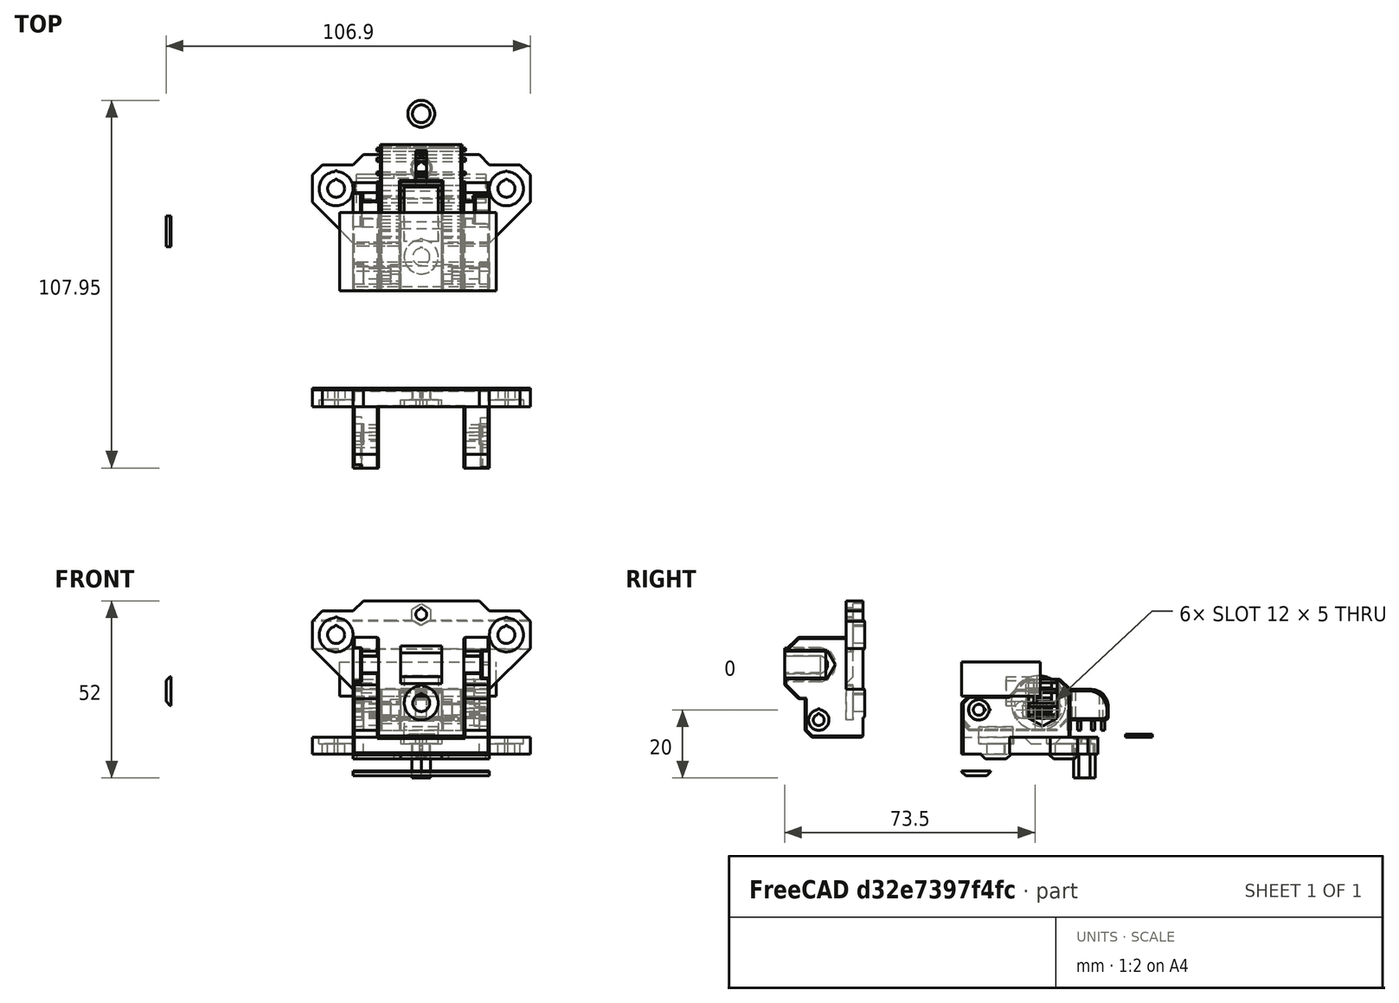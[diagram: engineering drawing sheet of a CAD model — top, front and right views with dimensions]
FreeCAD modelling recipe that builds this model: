
FCSTD DOCUMENT  (FreeCAD 0.18R14555 (Git shallow))
Label: y-idler-10mm-lower
License: All rights reserved
LicenseURL: http://en.wikipedia.org/wiki/All_rights_reserved
objects: Part::Box×62, Part::Cylinder×39, Part::Cut×31, Part::MultiFuse×30, Part::Chamfer×24, Part::Feature×21, Part::MultiCommon×1, Part::Fillet×1
note: 209 computed .brp shape members not serialized (recipe doc carries the construction recipe); baked Part::Feature solids carry a one-line shape summary decoded from their .brp

FEATURE [Part::Box] Box  label="Cube"
  AttacherType = Attacher::AttachEngine3D
  Height = 10
  Length = 40
  Placement = pos=(-20,-20,-10) rot=(0,0,1;0rad)
  Width = 40
FEATURE [Part::Box] Box001  label="Cube001"
  AttacherType = Attacher::AttachEngine3D
  Height = 12
  Length = 6
  Placement = pos=(6,-20,4) rot=(0,0,1;0rad)
  Width = 43
FEATURE [Part::Box] Box002  label="Cube002"
  AttacherType = Attacher::AttachEngine3D
  Height = 12
  Length = 6
  Placement = pos=(-12,-20,4) rot=(0,0,1;0rad)
  Width = 43
FEATURE [Part::Box] Box003  label="Cube003"
  AttacherType = Attacher::AttachEngine3D
  Height = 12
  Length = 12
  Placement = pos=(-6,12,2) rot=(0,0,1;0rad)
  Width = 11
FEATURE [Part::Cylinder] Cylinder  label="idler"
  Angle = 360
  AttacherType = Attacher::AttachEngine3D
  Height = 10
  Placement = pos=(5,2.54,10) rot=(0,-1,0;1.5708rad)
  Radius = 8
FEATURE [Part::Cylinder] Cylinder001
  Angle = 360
  AttacherType = Attacher::AttachEngine3D
  Height = 6
  Placement = pos=(6,-2,15) rot=(0,1,0;1.5708rad)
  Radius = 2.5
FEATURE [Part::Cylinder] Cylinder002
  Angle = 360
  AttacherType = Attacher::AttachEngine3D
  Height = 6
  Placement = pos=(-12,5,15) rot=(0,1,0;1.5708rad)
  Radius = 2.5
FEATURE [Part::Cylinder] Cylinder003
  Angle = 360
  AttacherType = Attacher::AttachEngine3D
  Height = 6
  Placement = pos=(-12,-2,15) rot=(0,1,0;1.5708rad)
  Radius = 2.5
FEATURE [Part::Cylinder] Cylinder004
  Angle = 360
  AttacherType = Attacher::AttachEngine3D
  Height = 6
  Placement = pos=(6,5,15) rot=(0,1,0;1.5708rad)
  Radius = 2.5
FEATURE [Part::Box] Box005  label="Cube005"
  AttacherType = Attacher::AttachEngine3D
  Height = 5
  Length = 6
  Placement = pos=(6,-2,12.5) rot=(0,0,1;0rad)
  Width = 7
FEATURE [Part::Box] Box006  label="Cube006"
  AttacherType = Attacher::AttachEngine3D
  Height = 5
  Length = 6
  Placement = pos=(-12,-2,12.5) rot=(0,0,1;0rad)
  Width = 7
FEATURE [Part::MultiFuse] Fusion
  Placement = pos=(0,2,-5) rot=(0,0,1;0rad)
  Shapes = -> [Box005,Cylinder001,Cylinder004]
FEATURE [Part::MultiFuse] Fusion001
  Placement = pos=(0,2,-5) rot=(0,0,1;0rad)
  Shapes = -> [Box006,Cylinder003,Cylinder002]
FEATURE [Part::Box] Box007  label="Cube007"
  AttacherType = Attacher::AttachEngine3D
  Height = 12
  Length = 7.5
  Placement = pos=(-20,-20,0) rot=(0,0,1;0rad)
  Width = 14
FEATURE [Part::Box] Box008  label="Cube008"
  AttacherType = Attacher::AttachEngine3D
  Height = 12
  Length = 7.5
  Placement = pos=(12.5,-20,0) rot=(0,0,1;0rad)
  Width = 14
FEATURE [Part::Box] Box009  label="Cube009"
  AttacherType = Attacher::AttachEngine3D
  Height = 20
  Length = 7.5
  Placement = pos=(-20,-10,0) rot=(0,0,1;0rad)
  Width = 18
FEATURE [Part::Box] Box010  label="Cube010"
  AttacherType = Attacher::AttachEngine3D
  Height = 20
  Length = 7.5
  Placement = pos=(12.5,-10,0) rot=(0,0,1;0rad)
  Width = 18
FEATURE [Part::Chamfer] Chamfer
  Base = -> Box009
  Edges = 2 edges r=4: [Edge10,Edge12]
FEATURE [Part::Chamfer] Chamfer001
  Base = -> Box010
  Edges = 2 edges r=4: [Edge10,Edge12]
FEATURE [Part::Cylinder] Cylinder005  label="Cylinder"
  Angle = 360
  AttacherType = Attacher::AttachEngine3D
  Height = 8
  Placement = pos=(-12,0,10) rot=(0,-1,0;1.5708rad)
  Radius = 2.6
FEATURE [Part::Cylinder] Cylinder006  label="Cylinder005"
  Angle = 360
  AttacherType = Attacher::AttachEngine3D
  Height = 8
  Placement = pos=(20,0,10) rot=(0,-1,0;1.5708rad)
  Radius = 2.6
FEATURE [Part::Box] Box011  label="Cube011"
  AttacherType = Attacher::AttachEngine3D
  Height = 10
  Length = 8
  Placement = pos=(12,-2.6,10) rot=(0,0,1;0rad)
  Width = 5.2
FEATURE [Part::Box] Box012  label="Cube012"
  AttacherType = Attacher::AttachEngine3D
  Height = 10
  Length = 8
  Placement = pos=(-20,-2.6,10) rot=(0,0,1;0rad)
  Width = 5.2
FEATURE [Part::Cylinder] Cylinder007  label="Cylinder006"
  Angle = 360
  AttacherType = Attacher::AttachEngine3D
  Height = 31
  Placement = pos=(0,16,-10) rot=(0,0,1;0rad)
  Radius = 1.6
FEATURE [Part::Box] Box013  label="Cube013"
  AttacherType = Attacher::AttachEngine3D
  Height = 30
  Length = 3.2
  Placement = pos=(-1.6,13.5,0) rot=(0,0,1;0rad)
  Width = 8
FEATURE [Part::Cylinder] Cylinder008  label="Cylinder007"
  Angle = 360
  AttacherType = Attacher::AttachEngine3D
  Height = 3
  Placement = pos=(25,10,-3) rot=(0,0,1;0rad)
  Radius = 5
FEATURE [Part::Cylinder] Cylinder009  label="Cylinder008"
  Angle = 360
  AttacherType = Attacher::AttachEngine3D
  Height = 8
  Placement = pos=(-12,-15,10) rot=(0,-1,0;1.5708rad)
  Radius = 1.6
FEATURE [Part::Cylinder] Cylinder010  label="Cylinder009"
  Angle = 360
  AttacherType = Attacher::AttachEngine3D
  Height = 8
  Placement = pos=(20,-15,10) rot=(0,-1,0;1.5708rad)
  Radius = 1.6
FEATURE [Part::Cylinder] Cylinder011  label="Cylinder010"
  Angle = 360
  AttacherType = Attacher::AttachEngine3D
  Height = 24
  Placement = pos=(12,-15,10) rot=(0,-1,0;1.5708rad)
  Radius = 1.6
FEATURE [Part::Cylinder] Cylinder012  label="Cylinder011"
  Angle = 360
  AttacherType = Attacher::AttachEngine3D
  Height = 3
  Placement = pos=(-25,10,-3) rot=(0,0,1;0rad)
  Radius = 5
FEATURE [Part::Box] Box014  label="Cube014"
  AttacherType = Attacher::AttachEngine3D
  Height = 10
  Length = 64
  Placement = pos=(-32,-6,-10) rot=(0,0,1;0rad)
  Width = 23
FEATURE [Part::Chamfer] Chamfer004
  Base = -> Box014
  Edges = 2 edges r=12: [Edge1,Edge5]
FEATURE [Part::Chamfer] Chamfer005
  Base = -> Box
  Edges = 2 edges r=3: [Edge3,Edge7]
FEATURE [Part::Chamfer] Chamfer006
  Base = -> Chamfer004
  Edges = 2 edges r=3: [Edge3,Edge13]
FEATURE [Part::Cylinder] Cylinder013  label="Cylinder012"
  Angle = 360
  AttacherType = Attacher::AttachEngine3D
  Height = 24
  Placement = pos=(12,-15,11.4) rot=(0,-1,0;1.5708rad)
  Radius = 0.5
FEATURE [Part::Cylinder] Cylinder014  label="Cylinder013"
  Angle = 360
  AttacherType = Attacher::AttachEngine3D
  Height = 8
  Placement = pos=(20,-13.6,10) rot=(0,-1,0;1.5708rad)
  Radius = 0.5
FEATURE [Part::Cylinder] Cylinder015  label="Cylinder014"
  Angle = 360
  AttacherType = Attacher::AttachEngine3D
  Height = 8
  Placement = pos=(-12,-13.6,10) rot=(0,-1,0;1.5708rad)
  Radius = 0.5
FEATURE [Part::Cylinder] Cylinder016  label="Cylinder015"
  Angle = 360
  AttacherType = Attacher::AttachEngine3D
  Height = 15
  Placement = pos=(-25,10,-10) rot=(0,0,1;0rad)
  Radius = 2.5
FEATURE [Part::Cylinder] Cylinder017  label="Cylinder016"
  Angle = 360
  AttacherType = Attacher::AttachEngine3D
  Height = 15
  Placement = pos=(25,10,-10) rot=(0,0,1;0rad)
  Radius = 2.5
FEATURE [Part::Cylinder] Cylinder018  label="Cylinder019"
  Angle = 360
  AttacherType = Attacher::AttachEngine3D
  Height = 15
  Placement = pos=(25,12.3,-10) rot=(0,0,1;0rad)
  Radius = 0.5
FEATURE [Part::Cylinder] Cylinder019  label="Cylinder020"
  Angle = 360
  AttacherType = Attacher::AttachEngine3D
  Height = 15
  Placement = pos=(-25,12.3,-10) rot=(0,0,1;0rad)
  Radius = 0.5
FEATURE [Part::Cylinder] Cylinder020  label="Cylinder021"
  Angle = 360
  AttacherType = Attacher::AttachEngine3D
  Height = 31
  Placement = pos=(0,17.4,-10) rot=(0,0,1;0rad)
  Radius = 0.5
FEATURE [Part::Cylinder] Cylinder021  label="Cylinder022"
  Angle = 360
  AttacherType = Attacher::AttachEngine3D
  Height = 15
  Placement = pos=(0,-10,-10) rot=(0,0,1;0rad)
  Radius = 2.5
FEATURE [Part::Cylinder] Cylinder022  label="Cylinder023"
  Angle = 360
  AttacherType = Attacher::AttachEngine3D
  Height = 3
  Placement = pos=(0,-10,0) rot=(0,0,1;0rad)
  Radius = 5
FEATURE [Part::Cylinder] Cylinder023  label="Cylinder024"
  Angle = 360
  AttacherType = Attacher::AttachEngine3D
  Height = 15
  Placement = pos=(0,-7.7,-10) rot=(0,0,1;0rad)
  Radius = 0.5
FEATURE [Part::MultiFuse] Fusion006
  Placement = pos=(0,0,-5) rot=(0,0,1;0rad)
  Shapes = -> [Cylinder023,Cylinder017,Cylinder021,Cylinder018,Cylinder020,Cylinder007,Cylinder016,Cylinder019]
FEATURE [Part::Cylinder] Cylinder024  label="Cylinder025"
  Angle = 360
  AttacherType = Attacher::AttachEngine3D
  Height = 2.5
  Placement = pos=(-17.5,0,10) rot=(0,-1,0;1.5708rad)
  Radius = 5
FEATURE [Part::Box] Box015  label="Cube015"
  AttacherType = Attacher::AttachEngine3D
  Height = 10
  Length = 2.5
  Placement = pos=(-20,-5,10) rot=(0,0,1;0rad)
  Width = 10
FEATURE [Part::Feature] Part__Feature  label="y_motor_mount v18"
  Placement = pos=(-68,0,0) rot=(0,0,1;0rad)
  shape: bbox 62 x 21 x 44 mm, 162 faces (baked)
FEATURE [Part::Box] Box016  label="Cube016"
  AttacherType = Attacher::AttachEngine3D
  Height = 10
  Length = 10
  Placement = pos=(-83.5,-7,9) rot=(0,0,1;0rad)
  Width = 9
FEATURE [Part::MultiCommon] Common
  Shapes = -> [Part__Feature,Box016]
FEATURE [Part::Feature] Common001
  Placement = pos=(13,-2.27,63.5) rot=(0.57735,-0.57735,0.57735;2.0944rad)
  shape: bbox 9 x 8.45 x 1.4 mm, 8 faces (baked)
FEATURE [Part::Feature] Common002
  Placement = pos=(4,-2.27,63.5) rot=(0.57735,-0.57735,0.57735;2.0944rad)
  shape: bbox 9 x 8.45 x 1.4 mm, 8 faces (baked)
FEATURE [Part::Feature] Common003
  Placement = pos=(-5,-2.27,63.5) rot=(0.57735,-0.57735,0.57735;2.0944rad)
  shape: bbox 9 x 8.45 x 1.4 mm, 8 faces (baked)
FEATURE [Part::Feature] Common004
  Placement = pos=(-14,-2.27,63.5) rot=(0.57735,-0.57735,0.57735;2.0944rad)
  shape: bbox 9 x 8.45 x 1.4 mm, 8 faces (baked)
FEATURE [Part::Feature] Common005
  Placement = pos=(-18,-2.27,63.5) rot=(0.57735,-0.57735,0.57735;2.0944rad)
  shape: bbox 9 x 8.45 x 1.4 mm, 8 faces (baked)
FEATURE [Part::MultiFuse] Fusion010
  Shapes = -> [Common001,Common002,Common003,Common005,Common004]
FEATURE [Part::Feature] Fusion010001  label="Fusion011"
  Placement = pos=(0,5.775,5) rot=(0,0,1;0rad)
  shape: bbox 40 x 8.45 x 1.4 mm, 38 faces (baked)
FEATURE [Part::Feature] Fusion010002  label="Fusion012"
  Placement = pos=(12,25.77,5) rot=(0,0,1;0rad)
  shape: bbox 40 x 8.45 x 1.4 mm, 38 faces (baked)
FEATURE [Part::Feature] Fusion010003  label="Fusion013"
  Placement = pos=(-12,25.765,5) rot=(0,0,1;0rad)
  shape: bbox 40 x 8.45 x 1.4 mm, 38 faces (baked)
FEATURE [Part::Cylinder] Cylinder025  label="Cylinder026"
  Angle = 360
  AttacherType = Attacher::AttachEngine3D
  Height = 3
  Placement = pos=(0,-10,-3) rot=(0,0,1;0rad)
  Radius = 5
FEATURE [Part::Cylinder] Cylinder026  label="Cylinder027"
  Angle = 360
  AttacherType = Attacher::AttachEngine3D
  Height = 3
  Placement = pos=(0,-5.2,-3) rot=(0,0,1;0rad)
  Radius = 0.5
FEATURE [Part::Cylinder] Cylinder027  label="Cylinder028"
  Angle = 360
  AttacherType = Attacher::AttachEngine3D
  Height = 3
  Placement = pos=(-25,14.8,-3) rot=(0,0,1;0rad)
  Radius = 0.5
FEATURE [Part::Cylinder] Cylinder028  label="Cylinder029"
  Angle = 360
  AttacherType = Attacher::AttachEngine3D
  Height = 3
  Placement = pos=(25,14.7,-3) rot=(0,0,1;0rad)
  Radius = 0.5
FEATURE [Part::MultiFuse] Fusion010005
  Shapes = -> [Cylinder025,Cylinder012,Cylinder008]
FEATURE [Part::Box] Box017  label="Cube017"
  AttacherType = Attacher::AttachEngine3D
  Height = 10
  Length = 10
  Placement = pos=(-60,0,-20) rot=(0,0,1;0rad)
  Width = 10
FEATURE [Part::Box] Box018  label="Cube018"
  AttacherType = Attacher::AttachEngine3D
  Height = 10
  Length = 10
  Placement = pos=(-40,0,-20) rot=(0,0,1;0rad)
  Width = 10
FEATURE [Part::Box] Box019  label="Cube019"
  AttacherType = Attacher::AttachEngine3D
  Height = 10
  Length = 10
  Placement = pos=(40,0,-20) rot=(0,0,1;0rad)
  Width = 10
FEATURE [Part::Box] Box020  label="Cube020"
  AttacherType = Attacher::AttachEngine3D
  Height = 10
  Length = 10
  Placement = pos=(40,0,-20) rot=(0,0,1;0rad)
  Width = 10
FEATURE [Part::Chamfer] Chamfer016
  Base = -> Box018
  Edges = 1 edges r=4: [Edge5]
  Placement = pos=(0,12,5) rot=(0,0,1;0rad)
FEATURE [Part::Chamfer] Chamfer017
  Base = -> Box017
  Edges = 1 edges r=4: [Edge7]
  Placement = pos=(20,-2,5) rot=(0,0,1;0rad)
FEATURE [Part::Chamfer] Chamfer018
  Base = -> Box019
  Edges = 1 edges r=4: [Edge3]
  Placement = pos=(-11,-3,5) rot=(0,0,1;0rad)
FEATURE [Part::Chamfer] Chamfer019
  Base = -> Box020
  Edges = 1 edges r=4: [Edge1]
  Placement = pos=(-9,11,5) rot=(0,0,1;0rad)
FEATURE [Part::Cylinder] Cylinder030  label="Cylinder031"
  Angle = 360
  AttacherType = Attacher::AttachEngine3D
  Height = 3
  Placement = pos=(-20,-12.2,10) rot=(0,1,0;1.5708rad)
  Radius = 0.5
FEATURE [Part::Cylinder] Cylinder031  label="Cylinder032"
  Angle = 360
  AttacherType = Attacher::AttachEngine3D
  Height = 3
  Placement = pos=(-20,-15,10) rot=(0,1,0;1.5708rad)
  Radius = 3
FEATURE [Part::Feature] Body005001  label="Body006"
  Placement = pos=(-9,-15,10) rot=(1,0,0;1.5708rad)
  shape: bbox 3 x 5.543 x 6.4 mm, 8 faces (baked)
FEATURE [Part::Cylinder] Cylinder032  label="Cylinder033"
  Angle = 360
  AttacherType = Attacher::AttachEngine3D
  Height = 3
  Placement = pos=(17,-15,10) rot=(0,1,0;1.5708rad)
  Radius = 3
FEATURE [Part::Cylinder] Cylinder033  label="Cylinder034"
  Angle = 360
  AttacherType = Attacher::AttachEngine3D
  Height = 3
  Placement = pos=(17,-12.2,10) rot=(0,1,0;1.5708rad)
  Radius = 0.5
FEATURE [Part::MultiFuse] Fusion010006003
  Shapes = -> [Cylinder031,Cylinder030]
FEATURE [Part::MultiFuse] Fusion010006004
  Shapes = -> [Cylinder033,Cylinder032]
FEATURE [Part::Feature] Body005002  label="Body007"
  Placement = pos=(6,-15,10) rot=(1,0,0;1.5708rad)
  shape: bbox 3 x 5.543 x 6.4 mm, 8 faces (baked)
FEATURE [Part::Feature] Body005003001  label="Body005004"
  Placement = pos=(0,16,-12) rot=(0,0,1;0rad)
  shape: bbox 5.543 x 6.4 x 10 mm, 8 faces (baked)
FEATURE [Part::Cylinder] Cylinder034  label="Cylinder035"
  Angle = 360
  AttacherType = Attacher::AttachEngine3D
  Height = 0.5
  Placement = pos=(0,16,-0.5) rot=(0,0,1;0rad)
  Radius = 3.2
FEATURE [Part::Cylinder] Cylinder035  label="Cylinder036"
  Angle = 360
  AttacherType = Attacher::AttachEngine3D
  Height = 0.5
  Placement = pos=(0,19,-0.5) rot=(0,0,1;0rad)
  Radius = 0.5
FEATURE [Part::MultiFuse] Fusion010006005
  Shapes = -> [Cylinder035,Cylinder034]
FEATURE [Part::Box] Box029  label="Cube029"
  AttacherType = Attacher::AttachEngine3D
  Height = 1
  Length = 2.1
  Placement = pos=(-20,-3.53,7.5) rot=(0,0,1;0rad)
  Width = 9.6
FEATURE [Part::Box] Box030  label="Cube030"
  AttacherType = Attacher::AttachEngine3D
  Height = 1
  Length = 4.1
  Placement = pos=(15.9,-2.68,5.6) rot=(0,0,1;0rad)
  Width = 7.91
FEATURE [Part::Box] Box032  label="Cube032"
  AttacherType = Attacher::AttachEngine3D
  Height = 1
  Length = 5
  Placement = pos=(-17.5,-1.13,7.5) rot=(0,0,1;0rad)
  Width = 4.8
FEATURE [Part::MultiFuse] Fusion010006008
  Shapes = -> [Box012,Cylinder005]
FEATURE [Part::MultiFuse] Fusion010006009
  Shapes = -> [Cylinder006,Box011]
FEATURE [Part::Cut] Cut022015
  Base = -> Chamfer
  Tool = -> Fusion010006008
FEATURE [Part::Cut] Cut022016
  Base = -> Chamfer001
  Tool = -> Fusion010006009
FEATURE [Part::Feature] Pad002001  label="Pad003"
  Placement = pos=(17.5,0,10) rot=(0.57735,0.57735,0.57735;2.0944rad)
  shape: bbox 10 x 8.314 x 9.6 mm, 8 faces (baked)
FEATURE [Part::Feature] Pad002002  label="Pad004"
  Placement = pos=(17.5,0,14) rot=(0.57735,0.57735,0.57735;2.0944rad)
  shape: bbox 10 x 8.314 x 9.6 mm, 8 faces (baked)
FEATURE [Part::Feature] Pad002003  label="Pad005"
  Placement = pos=(17.5,0,18) rot=(0.57735,0.57735,0.57735;2.0944rad)
  shape: bbox 10 x 8.314 x 9.6 mm, 8 faces (baked)
FEATURE [Part::MultiFuse] Fusion010006010
  Shapes = -> [Pad002003,Pad002001,Pad002002]
FEATURE [Part::Cut] Cut022017  label="base-right-arm-top"
  Base = -> Cut022016
  Placement = pos=(0,1.27,-2) rot=(0,0,1;0rad)
  Tool = -> Fusion010006010
FEATURE [Part::MultiFuse] Fusion010006011
  Shapes = -> [Cylinder024,Box015]
FEATURE [Part::Cut] Cut022018  label="base-left-arm-top"
  Base = -> Cut022015
  Placement = pos=(0,1.27,-2) rot=(0,0,1;0rad)
  Tool = -> Fusion010006011
FEATURE [Part::MultiFuse] Fusion010006014
  Shapes = -> [Cylinder013,Cylinder011]
FEATURE [Part::MultiFuse] Fusion010006015
  Placement = pos=(0,0,-2) rot=(0,0,1;0rad)
  Shapes = -> [Fusion010006014,Body005002,Body005001]
FEATURE [Part::MultiFuse] Fusion010006012003
  Placement = pos=(0,0,-2) rot=(0,0,1;0rad)
  Shapes = -> [Fusion010006003,Cylinder015,Cylinder009]
FEATURE [Part::MultiFuse] Fusion010006012004
  Placement = pos=(0,0,-2) rot=(0,0,1;0rad)
  Shapes = -> [Cylinder010,Cylinder014,Fusion010006004]
FEATURE [Part::MultiFuse] Fusion010006012005
  Shapes = -> [Chamfer006,Chamfer005]
FEATURE [Part::Box] Box038  label="Cube038"
  AttacherType = Attacher::AttachEngine3D
  Height = 5
  Length = 65
  Placement = pos=(-32,-24,-5) rot=(0,0,1;0rad)
  Width = 50
FEATURE [Part::Cut] Cut022020004
  Base = -> Fusion010006012005
  Placement = pos=(0,0,5) rot=(0,0,1;0rad)
  Tool = -> Box038
FEATURE [Part::MultiFuse] Fusion010006012006
  Shapes = -> [Fusion010003,Fusion010002,Cut022020004,Fusion010001]
FEATURE [Part::MultiFuse] Fusion010006012007
  Shapes = -> [Chamfer018,Chamfer019,Chamfer016,Chamfer017]
FEATURE [Part::Cut] Cut022020005
  Base = -> Fusion010006012006
  Tool = -> Fusion010006012007
FEATURE [Part::MultiFuse] Fusion010006012008
  Placement = pos=(0,0,1) rot=(0,0,1;0rad)
  Shapes = -> [Fusion010005,Cylinder027,Cylinder028,Cylinder026]
FEATURE [Part::Cut] Cut022020006
  Base = -> Cut022020005
  Tool = -> Fusion006
FEATURE [Part::Box] Box039  label="Cube039"
  AttacherType = Attacher::AttachEngine3D
  Height = 10
  Length = 40
  Placement = pos=(-26,-25,12) rot=(0,0,1;0rad)
  Width = 20
FEATURE [Part::Chamfer] Chamfer027
  Base = -> Box039
  Edges = 1 edges r=2: [Edge11]
  Placement = pos=(0,1,0) rot=(0,0,1;0rad)
FEATURE [Part::Box] Box040  label="Cube040"
  AttacherType = Attacher::AttachEngine3D
  Height = 10
  Length = 32
  Placement = pos=(-15,24,-8) rot=(0,0,1;0rad)
  Width = 26
FEATURE [Part::Chamfer] Chamfer028
  Base = -> Box040
  Edges = 1 edges r=3: [Edge10]
  Placement = pos=(0,-16,3) rot=(0,0,1;0rad)
FEATURE [Part::Box] Box041  label="Cube041"
  AttacherType = Attacher::AttachEngine3D
  Height = 10
  Length = 46
  Placement = pos=(-24,-20,12) rot=(0,0,1;0rad)
  Width = 23
FEATURE [Part::Box] Box043  label="cube042"
  AttacherType = Attacher::AttachEngine3D
  Height = 2.8
  Length = 26
  Placement = pos=(-13,11,2) rot=(0,0,1;0rad)
  Width = 1
FEATURE [Part::Feature] Chamfer030001  label="arm-rev-005"
  shape: bbox 24 x 43 x 12 mm, 56 faces (baked)
FEATURE [Part::Chamfer] Chamfer030003
  Base = -> Chamfer030001
  Edges = 1 edges r=1: [Edge50]
FEATURE [Part::Chamfer] Chamfer030004
  Base = -> Chamfer030003
  Edges = 24 edges r=0.4: [Edge31,Edge35,Edge55,Edge58,Edge62,Edge66,Edge69,Edge71,Edge72,Edge74,Edge76,Edge111,Edge112,Edge113,Edge114,Edge115,Edge116,Edge117,Edge118,Edge119,Edge120,Edge129,Edge131,Edge132]
FEATURE [Part::Box] Box044  label="Cube043"
  AttacherType = Attacher::AttachEngine3D
  Height = 4.6
  Length = 6
  Placement = pos=(-12,-2,5.7) rot=(0,0,1;0rad)
  Width = 1
FEATURE [Part::Box] Box045  label="Cube044"
  AttacherType = Attacher::AttachEngine3D
  Height = 4.6
  Length = 6
  Placement = pos=(6,-2,5.7) rot=(0,0,1;0rad)
  Width = 1
FEATURE [Part::Cylinder] Cylinder036  label="Cylinder037"
  Angle = 360
  AttacherType = Attacher::AttachEngine3D
  Height = 0.9
  Radius = 2.6
FEATURE [Part::Cylinder] Cylinder037  label="Cylinder038"
  Angle = 360
  AttacherType = Attacher::AttachEngine3D
  Height = 0.9
  Radius = 3.95
FEATURE [Part::Cut] Cut022020015  label="washer"
  Base = -> Cylinder037
  Placement = pos=(0,32,0) rot=(0,0,1;0rad)
  Tool = -> Cylinder036
FEATURE [Part::Box] Box046  label="Cube045"
  AttacherType = Attacher::AttachEngine3D
  Height = 3
  Length = 12
  Placement = pos=(-6,-4.23,0) rot=(0,0,1;0rad)
  Width = 11
FEATURE [Part::Chamfer] Chamfer030005
  Base = -> Box046
  Edges = 2 edges r=2: [Edge9,Edge11]
  Placement = pos=(0,2.54,-2) rot=(0,0,1;0rad)
FEATURE [Part::Feature] Fusion010006012010005001  label="base-rev-4-1-exp001"
  Placement = pos=(0,-54,20) rot=(1,0,0;1.5708rad)
  shape: bbox 64 x 24.4 x 40 mm, 166 faces, 5 solids (baked)
FEATURE [Part::Box] Box047  label="Cube046"
  AttacherType = Attacher::AttachEngine3D
  Height = 42
  Length = 68
  Placement = pos=(-32,-48.5,0) rot=(0,0,1;0rad)
  Width = 10
FEATURE [Part::Cut] Cut022020016002
  Base = -> Fusion010006012010005001
  Tool = -> Box047
FEATURE [Part::Box] Box048  label="cube043"
  AttacherType = Attacher::AttachEngine3D
  Height = 2.8
  Length = 26
  Placement = pos=(-13,14,2) rot=(0,0,1;0rad)
  Width = 1
FEATURE [Part::Box] Box049  label="cube044"
  AttacherType = Attacher::AttachEngine3D
  Height = 2.8
  Length = 26
  Placement = pos=(-13,21,2) rot=(0,0,1;0rad)
  Width = 1
FEATURE [Part::Box] Box051  label="cube046"
  AttacherType = Attacher::AttachEngine3D
  Height = 2.8
  Length = 26
  Placement = pos=(-13,18,2) rot=(0,0,1;0rad)
  Width = 1
FEATURE [Part::Box] Box052  label="Cube047"
  AttacherType = Attacher::AttachEngine3D
  Height = 4.6
  Length = 6
  Placement = pos=(-12,0,5.7) rot=(0,0,1;0rad)
  Width = 1
FEATURE [Part::Box] Box053  label="Cube048"
  AttacherType = Attacher::AttachEngine3D
  Height = 4.6
  Length = 6
  Placement = pos=(-12,2,5.7) rot=(0,0,1;0rad)
  Width = 1
FEATURE [Part::Box] Box054  label="Cube049"
  AttacherType = Attacher::AttachEngine3D
  Height = 4.6
  Length = 6
  Placement = pos=(-12,4,5.7) rot=(0,0,1;0rad)
  Width = 1
FEATURE [Part::Box] Box055  label="Cube050"
  AttacherType = Attacher::AttachEngine3D
  Height = 4.6
  Length = 6
  Placement = pos=(6,0,5.7) rot=(0,0,1;0rad)
  Width = 1
FEATURE [Part::Box] Box056  label="Cube051"
  AttacherType = Attacher::AttachEngine3D
  Height = 4.6
  Length = 6
  Placement = pos=(6,2,5.7) rot=(0,0,1;0rad)
  Width = 1
FEATURE [Part::Box] Box057  label="Cube052"
  AttacherType = Attacher::AttachEngine3D
  Height = 4.6
  Length = 6
  Placement = pos=(6,4,5.7) rot=(0,0,1;0rad)
  Width = 1
FEATURE [Part::Box] Box058  label="Cube053"
  AttacherType = Attacher::AttachEngine3D
  Height = 1
  Length = 4.1
  Placement = pos=(15.9,-2.68,9) rot=(0,0,1;0rad)
  Width = 7.91
FEATURE [Part::Box] Box059  label="Cube054"
  AttacherType = Attacher::AttachEngine3D
  Height = 1
  Length = 3
  Placement = pos=(12.5,-1.13,7.5) rot=(0,0,1;0rad)
  Width = 4.8
FEATURE [Part::Box] Box063  label="Cube058"
  AttacherType = Attacher::AttachEngine3D
  Height = 1
  Length = 3
  Placement = pos=(12.5,-1.13,10.5) rot=(0,0,1;0rad)
  Width = 4.8
FEATURE [Part::Box] Box064  label="Cube059"
  AttacherType = Attacher::AttachEngine3D
  Height = 1
  Length = 2.1
  Placement = pos=(-20,-3.53,10.5) rot=(0,0,1;0rad)
  Width = 9.6
FEATURE [Part::Box] Box066  label="Cube061"
  AttacherType = Attacher::AttachEngine3D
  Height = 1
  Length = 5
  Placement = pos=(-17.5,-1.13,10.5) rot=(0,0,1;0rad)
  Width = 4.8
FEATURE [Part::Box] Box068  label="Cube063"
  AttacherType = Attacher::AttachEngine3D
  Height = 1
  Length = 3
  Placement = pos=(12.5,-1.13,13.5) rot=(0,0,1;0rad)
  Width = 4.8
FEATURE [Part::Box] Box069  label="Cube064"
  AttacherType = Attacher::AttachEngine3D
  Height = 1
  Length = 2.1
  Placement = pos=(-20,-3.53,13.5) rot=(0,0,1;0rad)
  Width = 9.6
FEATURE [Part::Box] Box070  label="Cube065"
  AttacherType = Attacher::AttachEngine3D
  Height = 1
  Length = 2.1
  Placement = pos=(-20,-3.53,16) rot=(0,0,1;0rad)
  Width = 9.6
FEATURE [Part::Box] Box071  label="Cube066"
  AttacherType = Attacher::AttachEngine3D
  Height = 1
  Length = 5
  Placement = pos=(-17.5,-1.13,16) rot=(0,0,1;0rad)
  Width = 4.8
FEATURE [Part::Box] Box075  label="Cube070"
  AttacherType = Attacher::AttachEngine3D
  Height = 1
  Length = 3
  Placement = pos=(12.5,-1.13,16) rot=(0,0,1;0rad)
  Width = 4.8
FEATURE [Part::Box] Box076  label="Cube071"
  AttacherType = Attacher::AttachEngine3D
  Height = 1
  Length = 5
  Placement = pos=(-17.5,-1.13,13) rot=(0,0,1;0rad)
  Width = 4.8
FEATURE [Part::Box] Box077  label="Cube072"
  AttacherType = Attacher::AttachEngine3D
  Height = 1
  Length = 4.1
  Placement = pos=(15.9,-2.68,16) rot=(0,0,1;0rad)
  Width = 7.91
FEATURE [Part::Box] Box078  label="Cube073"
  AttacherType = Attacher::AttachEngine3D
  Height = 1
  Length = 4.1
  Placement = pos=(15.9,-2.68,13) rot=(0,0,1;0rad)
  Width = 7.91
FEATURE [Part::MultiFuse] Fusion010006012010005010  label="arm-custom-support"
  Shapes = -> [Box043,Box053,Box049,Box048,Box052,Box051,Box054,Box056,Box057,Box055,Box045,Box044]
FEATURE [Part::MultiFuse] Fusion010006012010005011  label="arm-rev-4-3"
  Shapes = -> [Fusion010006012010005010,Chamfer030004]
FEATURE [Part::Box] Box079  label="Cube074"
  AttacherType = Attacher::AttachEngine3D
  Height = 17
  Length = 10
  Placement = pos=(-21,-15,0) rot=(0,0,1;0rad)
  Width = 14
FEATURE [Part::Chamfer] Chamfer030006
  Base = -> Box079
  Edges = 1 edges r=10: [Edge11]
  Placement = pos=(0,2.27,12) rot=(0,0,1;0rad)
FEATURE [Part::Feature] Chamfer030006001  label="Chamfer030007"
  Placement = pos=(32,2.27,12) rot=(0,0,1;0rad)
  shape: bbox 10 x 14 x 17 mm, 7 faces (baked)
FEATURE [Part::Cut] Cut022020016004
  Base = -> Cut022018
  Tool = -> Chamfer030006
FEATURE [Part::Cut] Cut022020016005
  Base = -> Cut022017
  Tool = -> Chamfer030006001
FEATURE [Part::Box] Box080  label="Cube075"
  AttacherType = Attacher::AttachEngine3D
  Height = 10
  Length = 12
  Placement = pos=(-21,-5,17) rot=(0,0,1;0rad)
  Width = 16
FEATURE [Part::Cut] Cut022020016006  label="base-left-arm-top-trim"
  Base = -> Cut022020016004
  Placement = pos=(0,2.54,0) rot=(0,0,1;0rad)
  Tool = -> Box080
FEATURE [Part::Box] Box081  label="Cube076"
  AttacherType = Attacher::AttachEngine3D
  Height = 10
  Length = 12
  Placement = pos=(9,-5,17) rot=(0,0,1;0rad)
  Width = 16
FEATURE [Part::Cut] Cut022020016007  label="base-right-arm-top-trim"
  Base = -> Cut022020016005
  Placement = pos=(0,2.54,0) rot=(0,0,1;0rad)
  Tool = -> Box081
FEATURE [Part::MultiFuse] Fusion010006012010005014
  Shapes = -> [Box071,Box076,Box066,Box032]
FEATURE [Part::MultiFuse] Fusion010006012010005016
  Shapes = -> [Box029,Box064,Box069,Box070]
FEATURE [Part::Box] Box082  label="Cube077"
  AttacherType = Attacher::AttachEngine3D
  Height = 14
  Length = 2
  Placement = pos=(17.55,-3.1,3) rot=(0,0,1;0rad)
  Width = 9
FEATURE [Part::Feature] Chamfer030006002001  label="arm-rev-4-3-no-support001"
  shape: bbox 64 x 40 x 23.4 mm, 138 faces (baked)
FEATURE [Part::Cut] Cut022020016008
  Base = -> Box082
  Placement = pos=(-2.05,2.54,0) rot=(0,0,1;0rad)
  Tool = -> Chamfer030006002001
FEATURE [Part::MultiFuse] Fusion010006012010005012002
  Shapes = -> [Box059,Box075,Box063,Box068]
FEATURE [Part::MultiFuse] Fusion010006012010005012003
  Shapes = -> [Box030,Box078,Box058,Box077]
FEATURE [Part::MultiFuse] Fusion010006012010005012004  label="base-custom-support"
  Placement = pos=(0,2.54,0) rot=(0,0,1;0rad)
  Shapes = -> [Fusion010006012010005016,Fusion010006012010005012002,Fusion010006012010005012003,Fusion010006012010005014]
FEATURE [Part::Box] Box083  label="Cube078"
  AttacherType = Attacher::AttachEngine3D
  Height = 10
  Length = 12
  Placement = pos=(-6,-15,-15) rot=(0,0,1;0rad)
  Width = 10
FEATURE [Part::Box] Box084  label="Cube079"
  AttacherType = Attacher::AttachEngine3D
  Height = 10
  Length = 13
  Placement = pos=(19,5,-15) rot=(0,0,1;0rad)
  Width = 10
FEATURE [Part::Box] Box085  label="Cube080"
  AttacherType = Attacher::AttachEngine3D
  Height = 10
  Length = 13
  Placement = pos=(-32,5,-15) rot=(0,0,1;0rad)
  Width = 10
FEATURE [Part::Cut] Cut022020016013
  Base = -> Box007
  Tool = -> Fusion010006012003
FEATURE [Part::Chamfer] Chamfer030006002002  label="base-left-arm-bottom"
  Base = -> Cut022020016013
  Edges = 1 edges r=2: [Edge10]
FEATURE [Part::Cut] Cut022020016018
  Base = -> Box008
  Tool = -> Fusion010006012004
FEATURE [Part::Chamfer] Chamfer030006002003  label="base-right-arm-bottom"
  Base = -> Cut022020016018
  Edges = 1 edges r=2: [Edge10]
FEATURE [Part::Cut] Cut022020016019  label="base-right-arm-top-cut"
  Base = -> Cut022020016007
  Tool = -> Cut022020016008
FEATURE [Part::Cylinder] Cylinder038  label="Cylinder039"
  Angle = 360
  AttacherType = Attacher::AttachEngine3D
  Height = 10
  Placement = pos=(0,16,-12) rot=(0,0,1;0rad)
  Radius = 2.7
FEATURE [Part::Cylinder] Cylinder039  label="Cylinder040"
  Angle = 360
  AttacherType = Attacher::AttachEngine3D
  Height = 10
  Placement = pos=(0,18.5,-12) rot=(0,0,1;0rad)
  Radius = 0.5
FEATURE [Part::Cut] Cut022020016020
  Base = -> Cut022020006
  Tool = -> Chamfer030005
FEATURE [Part::Cut] Cut022020016021
  Base = -> Cut022020016020
  Tool = -> Fusion010006012008
FEATURE [Part::Cut] Cut022020016022
  Base = -> Cut022020016021
  Tool = -> Cylinder038
FEATURE [Part::Cut] Cut022020016023
  Base = -> Cut022020016022
  Tool = -> Box083
FEATURE [Part::Cut] Cut022020016024
  Base = -> Cut022020016023
  Tool = -> Box084
FEATURE [Part::Cut] Cut022020016025
  Base = -> Cut022020016024
  Tool = -> Box085
FEATURE [Part::Cut] Cut022020016026
  Base = -> Cut022020016025
  Tool = -> Cylinder039
FEATURE [Part::MultiFuse] Fusion010006012010005012005  label="base"
  Shapes = -> [Chamfer030006002002,Cut022020016006,Cut022020016019,Chamfer030006002003,Cut022020016026]
FEATURE [Part::Feature] Fusion010006012010005012005001  label="base001"
  shape: bbox 64 x 40 x 23.4 mm, 108 faces (baked)
FEATURE [Part::Chamfer] Chamfer030006002004
  Base = -> Fusion010006012010005012005001
  Edges = 36 edges r=0.4: [Edge2,Edge4,Edge6,Edge8,Edge9,Edge19,Edge21,Edge22,Edge24,Edge25,Edge27,Edge30,Edge31,Edge33,Edge34,Edge37,Edge38,Edge40,Edge50,Edge52,Edge54,Edge55,Edge75,Edge116,Edge117,Edge147,Edge148,Edge149,Edge150,Edge152,Edge154,Edge166,Edge173,Edge174,Edge175,Edge176]
FEATURE [Part::MultiFuse] Fusion010006012010005012005002  label="base-rev-4"
  Shapes = -> [Fusion010006012010005012004,Chamfer030006002004]
FEATURE [Part::Cut] Cut
  Base = -> Box002
  Placement = pos=(0,0,-2) rot=(0,0,1;0rad)
  Tool = -> Fusion001
FEATURE [Part::Cut] Cut022020016027
  Base = -> Box001
  Placement = pos=(0,0,-2) rot=(0,0,1;0rad)
  Tool = -> Fusion
FEATURE [Part::MultiFuse] Fusion010006012010005012005003
  Shapes = -> [Cut022020016027,Box003,Cut]
FEATURE [Part::Fillet] Fillet
  Base = -> Fusion010006012010005012005003
  Edges = 3 edges r=6: [Edge16,Edge33,Edge46]
FEATURE [Part::Cut] Cut022020016028
  Base = -> Fillet
  Tool = -> Box013
FEATURE [Part::Cut] Cut022020016029
  Base = -> Cut022020016028
  Tool = -> Chamfer027
FEATURE [Part::Cut] Cut022020016030
  Base = -> Cut022020016029
  Tool = -> Chamfer028
FEATURE [Part::Chamfer] Chamfer030006002005
  Base = -> Cut022020016030
  Edges = 3 edges r=0.5: [Edge38,Edge42,Edge43]
FEATURE [Part::Cut] Cut022020016031
  Base = -> Chamfer030006002005
  Tool = -> Fusion010006015
FEATURE [Part::Chamfer] Chamfer030006002006
  Base = -> Cut022020016031
  Edges = 2 edges r=2: [Edge84,Edge129]
FEATURE [Part::Chamfer] Chamfer030006002007
  Base = -> Chamfer030006002006
  Edges = 2 edges r=3: [Edge26,Edge147]
FEATURE [Part::Box] Box086  label="Cube081"
  AttacherType = Attacher::AttachEngine3D
  Height = 4
  Length = 3.2
  Placement = pos=(-1.6,18,14.4) rot=(0,0,1;0rad)
  Width = 4
FEATURE [Part::Chamfer] Chamfer030006002009
  Base = -> Chamfer030006002007
  Edges = 1 edges r=1: [Edge44]
FEATURE [Part::Chamfer] Chamfer030006002010
  Base = -> Box086
  Edges = 1 edges r=3: [Edge11]
  Placement = pos=(0,1,-5) rot=(0,0,1;0rad)
FEATURE [Part::Cut] Cut022020016032  label="arm-rev-4"
  Base = -> Chamfer030006002009
  Tool = -> Chamfer030006002010
FEATURE [Part::Feature] Cut022020016032001  label="arm-rev-006"
  shape: bbox 24 x 43 x 12 mm, 56 faces (baked)
FEATURE [Part::Chamfer] Chamfer030006002011
  Base = -> Cut022020016032001
  Edges = 42 edges r=0.4: [Edge5,Edge8,Edge10,Edge11,Edge19,Edge20,Edge21,Edge22,Edge23,Edge24,Edge26,Edge27,Edge28,Edge29,Edge37,Edge39,Edge40,Edge41,Edge42,Edge43,Edge44,Edge45,Edge58,Edge59,Edge60,Edge61,Edge62,Edge63,Edge64,Edge65,Edge66,Edge67,Edge68,Edge69,Edge77,Edge78,Edge79,Edge80,Edge81,Edge82,Edge83,Edge84]
